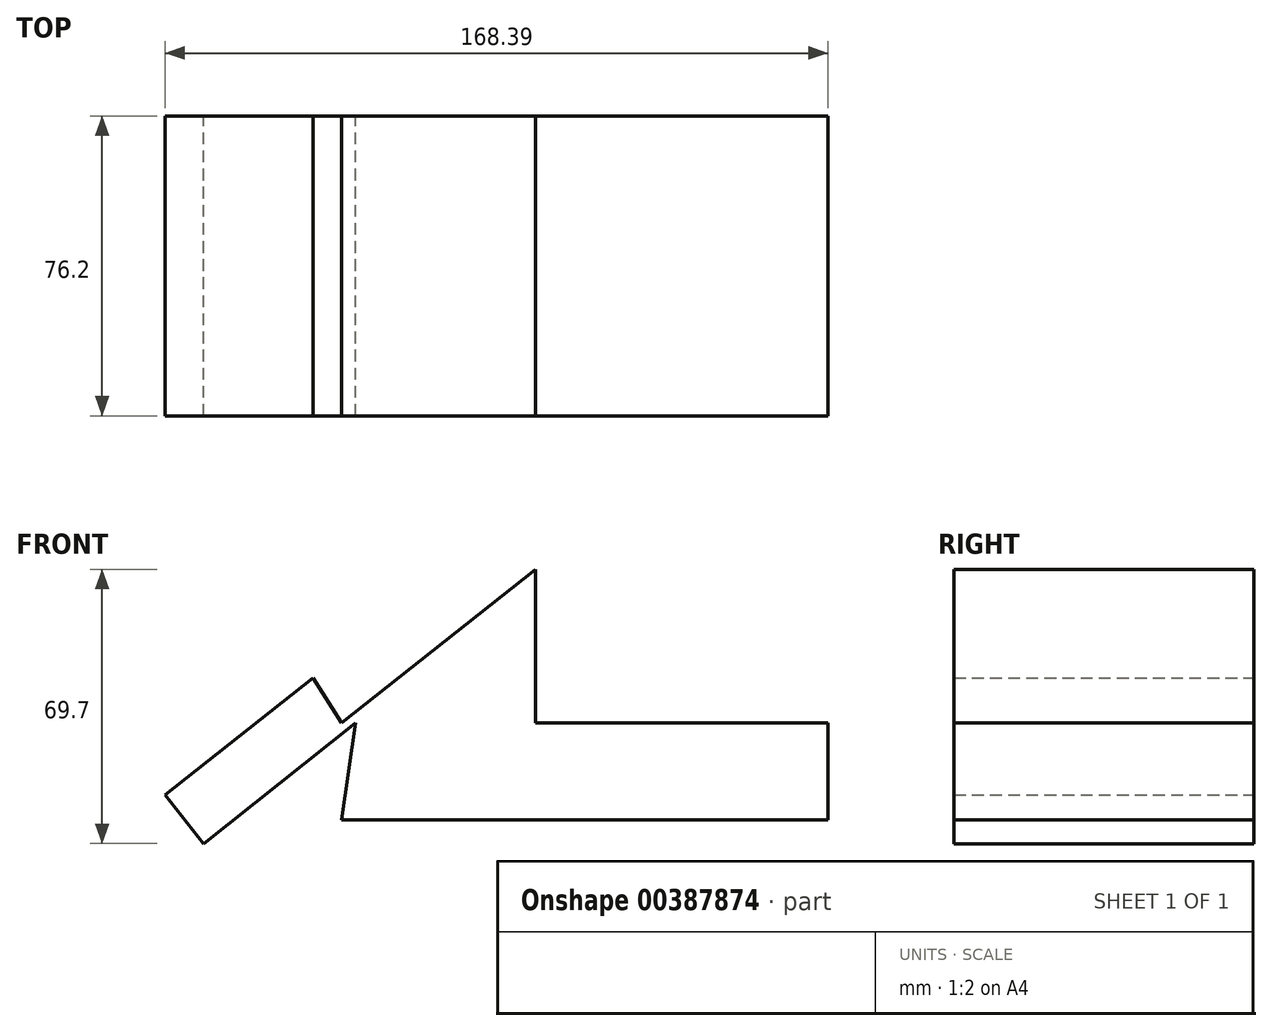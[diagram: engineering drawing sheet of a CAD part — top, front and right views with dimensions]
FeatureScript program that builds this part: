
annotation { "Feature Type Name" : "Feature", "Feature Type Description" : "" }
export const myFeature = defineFeature(function(context is Context, id is Id, definition is map)
    precondition{}
    {
        {
            var Q0;
            Q0=qCreatedBy(makeId("Front.planeOp"),FACE);
            var sketch = newSketch(context, id + "F0", { "sketchPlane" : qUnion([Q0])});
            skLineSegment(sketch, "E0", {"start": v(-64.27, 34.26) * mm, "end": v(-15.07, 73.3) * mm});
            skLineSegment(sketch, "E1", {"start": v(-15.07, 73.3) * mm, "end": v(-15.07, 34.26) * mm});
            skLineSegment(sketch, "E2", {"start": v(-15.07, 34.26) * mm, "end": v(59.24, 34.26) * mm});
            skLineSegment(sketch, "E3", {"start": v(59.24, 34.26) * mm, "end": v(59.24, 9.7) * mm});
            skLineSegment(sketch, "E4", {"start": v(59.24, 9.7) * mm, "end": v(-64.27, 9.7) * mm});
            skLineSegment(sketch, "E5", {"start": v(-64.27, 9.7) * mm, "end": v(-60.71, 34.26) * mm});
            skLineSegment(sketch, "E6", {"start": v(-60.71, 34.26) * mm, "end": v(-99.36, 3.6) * mm});
            skLineSegment(sketch, "E7", {"start": v(-99.36, 3.6) * mm, "end": v(-109.15, 15.93) * mm});
            skLineSegment(sketch, "E8", {"start": v(-109.15, 15.93) * mm, "end": v(-71.58, 45.74) * mm});
            skLineSegment(sketch, "E9", {"start": v(-71.58, 45.74) * mm, "end": v(-64.27, 34.26) * mm});
            skLineSegment(sketch, "E10", {"start": v(-71.58, 45.74) * mm, "end": v(-66.64, 49.66) * mm});
            skSolve(sketch);
        }
        {
            var Q0;
            Q0=makeQuery(id+"F0.imprint","IMPRINT",FACE,{"disambiguationData":[TD([[makeQuery(id+"F0.imprint","IMPRINT",EDGE,{"derivedFrom":sQuery(id+"F0.wireOp",EDGE,"E0")}),-1.0]])]});
            extrude(context, id + "F1", {"entities" : qUnion([Q0]), "endBound" : BoundingType.SYMMETRIC, "depth" : 76.2 * mm});
        }
    });
